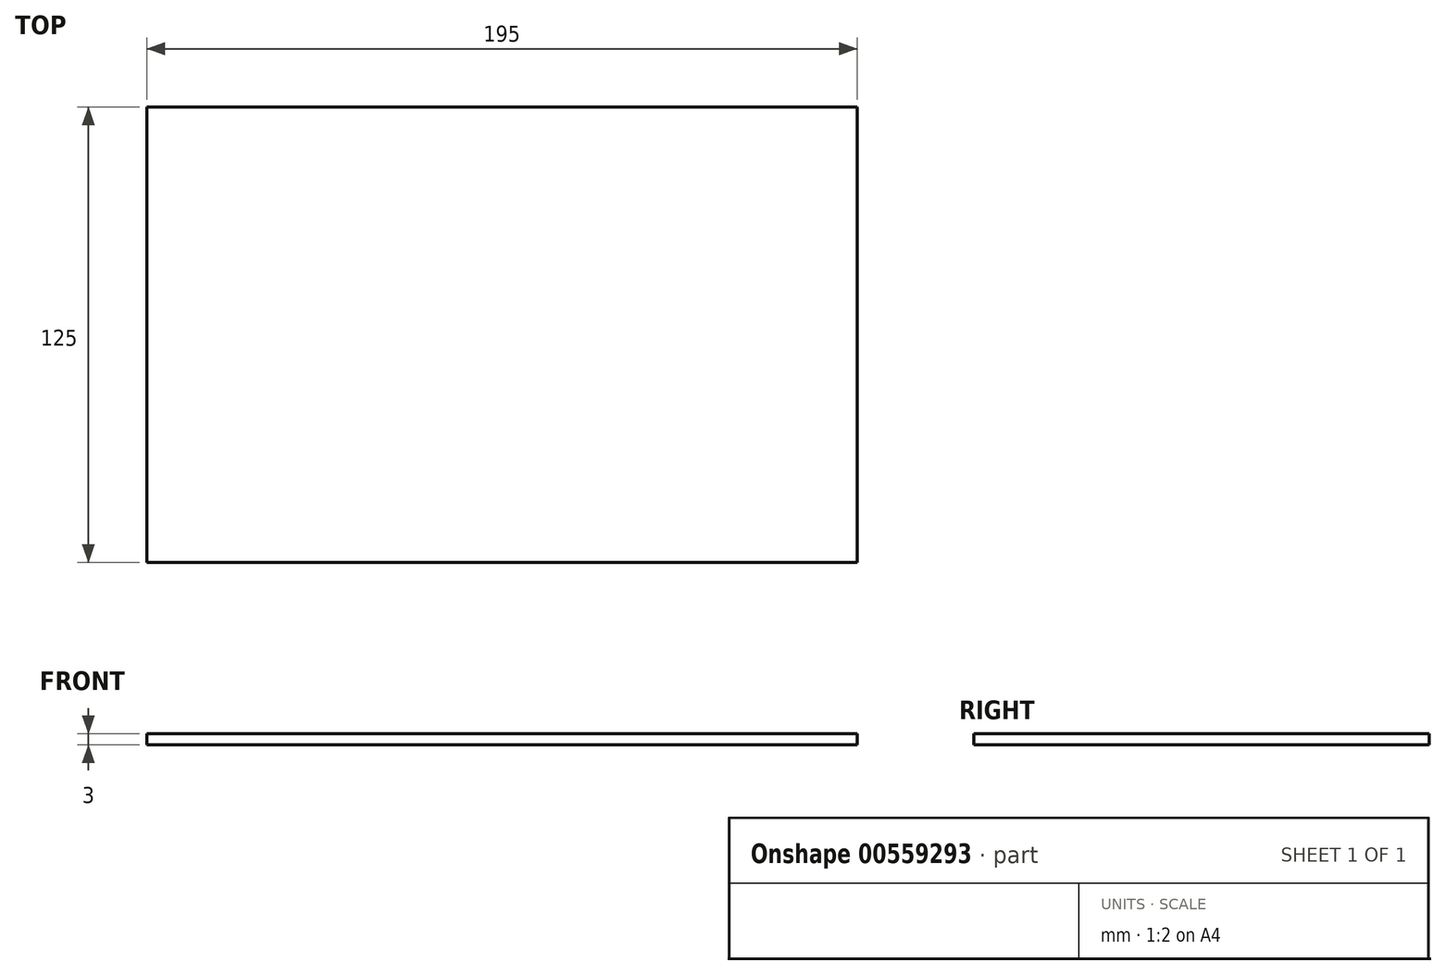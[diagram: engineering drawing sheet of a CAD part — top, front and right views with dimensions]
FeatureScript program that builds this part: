
annotation { "Feature Type Name" : "Feature", "Feature Type Description" : "" }
export const myFeature = defineFeature(function(context is Context, id is Id, definition is map)
    precondition{}
    {
        {
            var Q0;
            Q0=qCreatedBy(makeId("Top.planeOp"),FACE);
            var sketch = newSketch(context, id + "F0", { "sketchPlane" : qUnion([Q0])});
            skLineSegment(sketch, "E0.bottom", {"start": v(97.5, -62.5) * mm, "end": v(-97.5, -62.5) * mm});
            skLineSegment(sketch, "E0.top", {"start": v(97.5, 62.5) * mm, "end": v(-97.5, 62.5) * mm});
            skLineSegment(sketch, "E0.left", {"start": v(97.5, -62.5) * mm, "end": v(97.5, 62.5) * mm});
            skLineSegment(sketch, "E0.right", {"start": v(-97.5, -62.5) * mm, "end": v(-97.5, 62.5) * mm});
            skPoint(sketch, "E0.middle", {"position": v(0, 0) * mm});
            skSolve(sketch);
        }
        {
            var Q0;
            Q0 = qSketchRegion(id + "F0", true);
            extrude(context, id + "F1", {"entities" : qUnion([Q0]), "depth" : 3 * mm, "offsetDistance" : 25.4 * mm});
        }
    });
